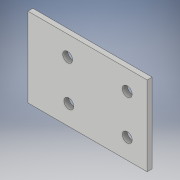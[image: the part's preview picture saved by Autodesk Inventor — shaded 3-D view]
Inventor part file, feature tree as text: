
AUTODESK INVENTOR PART (.ipt)
format: ipt  version: 2017 (Build 210142000, 142)  size: 106,496 bytes
history: native  units: in
note: dims shown in document units (in); Inventor stores cm internally (conversion verified against a paired STEP export)
features: extrude x1, sketch x1
ambient origin geometry x8: Origin, YZ Plane, XZ Plane, XY Plane, X Axis, Y Axis, Z Axis, Center Point
bodies: Solid1 (feature_tree)
feature tree (2):
  extrude  "Extrusion1"  Depth=2.0in
  sketch  "Sketch1"  dims[d0=3.0in d1=2.0in d2=0.25in d3=0.25in d4=1.0in d5=0.5in d6=1.0in d7=0.25in d8=0.25in d9=1.0in d10=0.125in d11=0.0in d12=0.5in d13=0.5in d14=0.5in]
